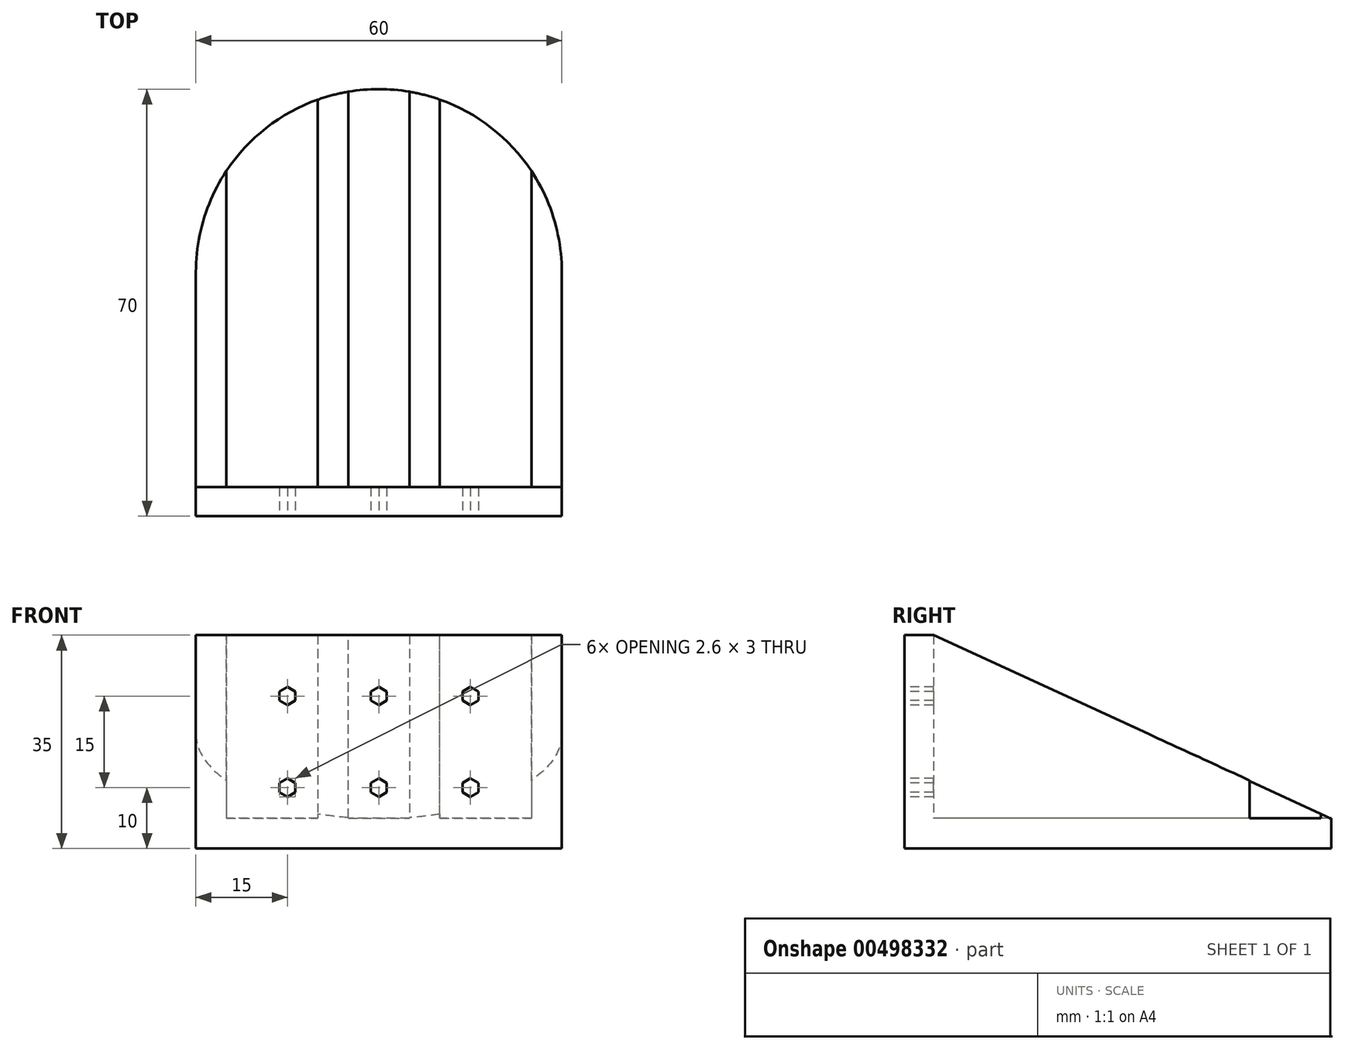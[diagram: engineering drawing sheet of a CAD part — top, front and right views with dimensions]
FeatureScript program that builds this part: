
annotation { "Feature Type Name" : "Feature", "Feature Type Description" : "" }
export const myFeature = defineFeature(function(context is Context, id is Id, definition is map)
    precondition{}
    {
        {
            var Q0;
            Q0=qCreatedBy(makeId("Top.planeOp"),FACE);
            var sketch = newSketch(context, id + "F0", { "sketchPlane" : qUnion([Q0])});
            skLineSegment(sketch, "E0.bottom", {"start": v(0, 0) * mm, "end": v(60, 0) * mm});
            skLineSegment(sketch, "E0.top", {"start": v(0, 70) * mm, "end": v(60, 70) * mm});
            skLineSegment(sketch, "E0.left", {"start": v(0, 0) * mm, "end": v(0, 70) * mm});
            skLineSegment(sketch, "E0.right", {"start": v(60, 0) * mm, "end": v(60, 70) * mm});
            skSolve(sketch);
        }
        {
            var Q0;
            Q0=makeQuery(id+"F0.imprint","IMPRINT",FACE,{"disambiguationData":[TD([[makeQuery(id+"F0.imprint","IMPRINT",EDGE,{"derivedFrom":sQuery(id+"F0.wireOp",EDGE,"E0.bottom")}),1.0]])]});
            extrude(context, id + "F1", {"entities" : qUnion([Q0]), "depth" : 5 * mm});
        }
        {
            var Q0;
            Q0=makeQuery(id+"F1.opExtrude","CAP_FACE",FACE,{"disambiguationData":[OSD([sQuery(id+"F0.wireOp",EDGE,"E0.bottom"),sQuery(id+"F0.wireOp",EDGE,"E0.top"),sQuery(id+"F0.wireOp",EDGE,"E0.left"),sQuery(id+"F0.wireOp",EDGE,"E0.right")])],"isStart":false});
            var sketch = newSketch(context, id + "F2", { "sketchPlane" : qUnion([Q0])});
            skLineSegment(sketch, "E1.bottom", {"start": v(0, 0) * mm, "end": v(60, 0) * mm});
            skLineSegment(sketch, "E1.top", {"start": v(0, 4.74) * mm, "end": v(60, 4.74) * mm});
            skLineSegment(sketch, "E1.left", {"start": v(0, 0) * mm, "end": v(0, 4.74) * mm});
            skLineSegment(sketch, "E1.right", {"start": v(60, 0) * mm, "end": v(60, 4.74) * mm});
            skSolve(sketch);
        }
        {
            var Q0;
            Q0 = qSketchRegion(id + "F2", true);
            extrude(context, id + "F3", {"entities" : qUnion([Q0]), "operationType" : NewBodyOperationType.ADD, "depth" : 30 * mm});
        }
        {
            var Q0;
            Q0=makeQuery(id+"F3.boolean.opBoolean","MERGE",FACE,{"derivedFrom":[makeQuery(id+"F1.opExtrude","SWEPT_FACE",FACE,{"disambiguationData":[OSD([sQuery(id+"F0.wireOp",EDGE,"E0.bottom")])]}),makeQuery(id+"F3.opExtrude","SWEPT_FACE",FACE,{"disambiguationData":[OSD([sQuery(id+"F2.wireOp",EDGE,"E1.bottom")])]})]});
            var sketch = newSketch(context, id + "F4", { "sketchPlane" : qUnion([Q0])});
            skLineSegment(sketch, "E2", {"start": v(0, 0) * mm, "end": v(30, 0) * mm});
            skLineSegment(sketch, "E3", {"start": v(30, 0) * mm, "end": v(30, 10) * mm});
            skLineSegment(sketch, "E4", {"start": v(30, 10) * mm, "end": v(45, 10) * mm});
            skLineSegment(sketch, "E5", {"start": v(45, 10) * mm, "end": v(30, 10) * mm});
            skLineSegment(sketch, "E6", {"start": v(30, 10) * mm, "end": v(15, 10) * mm});
            skLineSegment(sketch, "E7", {"start": v(15, 10) * mm, "end": v(15, 25) * mm});
            skLineSegment(sketch, "E8", {"start": v(15, 25) * mm, "end": v(30, 25) * mm});
            skLineSegment(sketch, "E9", {"start": v(30, 25) * mm, "end": v(45, 25) * mm});
            skLineSegment(sketch, "E10", {"start": v(15, 25) * mm, "end": v(15, 26.5) * mm});
            skCircle(sketch, "E11.cCircle", {"center": v(15, 25) * mm, "radius": 1.5 * mm, "construction": true});
            skLineSegment(sketch, "E11.0", {"start": v(15, 26.5) * mm, "end": v(16.3, 25.75) * mm});
            skLineSegment(sketch, "E11.1", {"start": v(16.3, 25.75) * mm, "end": v(16.3, 24.25) * mm});
            skLineSegment(sketch, "E11.2", {"start": v(16.3, 24.25) * mm, "end": v(15, 23.5) * mm});
            skLineSegment(sketch, "E11.3", {"start": v(15, 23.5) * mm, "end": v(13.7, 24.25) * mm});
            skLineSegment(sketch, "E11.4", {"start": v(13.7, 24.25) * mm, "end": v(13.7, 25.75) * mm});
            skLineSegment(sketch, "E11.5", {"start": v(13.7, 25.75) * mm, "end": v(15, 26.5) * mm});
            skLineSegment(sketch, "E12.0.1.0", {"start": v(16.3, 9.25) * mm, "end": v(15, 8.5) * mm});
            skLineSegment(sketch, "E12.0.1.1", {"start": v(16.3, 10.75) * mm, "end": v(16.3, 9.25) * mm});
            skLineSegment(sketch, "E12.0.1.2", {"start": v(15, 11.5) * mm, "end": v(16.3, 10.75) * mm});
            skCircle(sketch, "E12.0.1.3", {"center": v(15, 10) * mm, "radius": 1.5 * mm, "construction": true});
            skLineSegment(sketch, "E12.0.1.4", {"start": v(15, 8.5) * mm, "end": v(13.7, 9.25) * mm});
            skLineSegment(sketch, "E12.0.1.5", {"start": v(13.7, 9.25) * mm, "end": v(13.7, 10.75) * mm});
            skLineSegment(sketch, "E12.0.1.6", {"start": v(13.7, 10.75) * mm, "end": v(15, 11.5) * mm});
            skLineSegment(sketch, "E12.0.1.7", {"start": v(15, 10) * mm, "end": v(15, 11.5) * mm});
            skLineSegment(sketch, "E12.1.0.0", {"start": v(31.3, 24.25) * mm, "end": v(30, 23.5) * mm});
            skLineSegment(sketch, "E12.1.0.1", {"start": v(31.3, 25.75) * mm, "end": v(31.3, 24.25) * mm});
            skLineSegment(sketch, "E12.1.0.2", {"start": v(30, 26.5) * mm, "end": v(31.3, 25.75) * mm});
            skCircle(sketch, "E12.1.0.3", {"center": v(30, 25) * mm, "radius": 1.5 * mm, "construction": true});
            skLineSegment(sketch, "E12.1.0.4", {"start": v(30, 23.5) * mm, "end": v(28.7, 24.25) * mm});
            skLineSegment(sketch, "E12.1.0.5", {"start": v(28.7, 24.25) * mm, "end": v(28.7, 25.75) * mm});
            skLineSegment(sketch, "E12.1.0.6", {"start": v(28.7, 25.75) * mm, "end": v(30, 26.5) * mm});
            skLineSegment(sketch, "E12.1.0.7", {"start": v(30, 25) * mm, "end": v(30, 26.5) * mm});
            skLineSegment(sketch, "E12.1.1.0", {"start": v(31.3, 9.25) * mm, "end": v(30, 8.5) * mm});
            skLineSegment(sketch, "E12.1.1.1", {"start": v(31.3, 10.75) * mm, "end": v(31.3, 9.25) * mm});
            skLineSegment(sketch, "E12.1.1.2", {"start": v(30, 11.5) * mm, "end": v(31.3, 10.75) * mm});
            skCircle(sketch, "E12.1.1.3", {"center": v(30, 10) * mm, "radius": 1.5 * mm, "construction": true});
            skLineSegment(sketch, "E12.1.1.4", {"start": v(30, 8.5) * mm, "end": v(28.7, 9.25) * mm});
            skLineSegment(sketch, "E12.1.1.5", {"start": v(28.7, 9.25) * mm, "end": v(28.7, 10.75) * mm});
            skLineSegment(sketch, "E12.1.1.6", {"start": v(28.7, 10.75) * mm, "end": v(30, 11.5) * mm});
            skLineSegment(sketch, "E12.1.1.7", {"start": v(30, 10) * mm, "end": v(30, 11.5) * mm});
            skLineSegment(sketch, "E12.2.0.0", {"start": v(46.3, 24.25) * mm, "end": v(45, 23.5) * mm});
            skLineSegment(sketch, "E12.2.0.1", {"start": v(46.3, 25.75) * mm, "end": v(46.3, 24.25) * mm});
            skLineSegment(sketch, "E12.2.0.2", {"start": v(45, 26.5) * mm, "end": v(46.3, 25.75) * mm});
            skCircle(sketch, "E12.2.0.3", {"center": v(45, 25) * mm, "radius": 1.5 * mm, "construction": true});
            skLineSegment(sketch, "E12.2.0.4", {"start": v(45, 23.5) * mm, "end": v(43.7, 24.25) * mm});
            skLineSegment(sketch, "E12.2.0.5", {"start": v(43.7, 24.25) * mm, "end": v(43.7, 25.75) * mm});
            skLineSegment(sketch, "E12.2.0.6", {"start": v(43.7, 25.75) * mm, "end": v(45, 26.5) * mm});
            skLineSegment(sketch, "E12.2.0.7", {"start": v(45, 25) * mm, "end": v(45, 26.5) * mm});
            skLineSegment(sketch, "E12.2.1.0", {"start": v(46.3, 9.25) * mm, "end": v(45, 8.5) * mm});
            skLineSegment(sketch, "E12.2.1.1", {"start": v(46.3, 10.75) * mm, "end": v(46.3, 9.25) * mm});
            skLineSegment(sketch, "E12.2.1.2", {"start": v(45, 11.5) * mm, "end": v(46.3, 10.75) * mm});
            skCircle(sketch, "E12.2.1.3", {"center": v(45, 10) * mm, "radius": 1.5 * mm, "construction": true});
            skLineSegment(sketch, "E12.2.1.4", {"start": v(45, 8.5) * mm, "end": v(43.7, 9.25) * mm});
            skLineSegment(sketch, "E12.2.1.5", {"start": v(43.7, 9.25) * mm, "end": v(43.7, 10.75) * mm});
            skLineSegment(sketch, "E12.2.1.6", {"start": v(43.7, 10.75) * mm, "end": v(45, 11.5) * mm});
            skLineSegment(sketch, "E12.2.1.7", {"start": v(45, 10) * mm, "end": v(45, 11.5) * mm});
            skLineSegment(sketch, "E12.direction1", {"start": v(13.7, 24.25) * mm, "end": v(28.7, 24.25) * mm, "construction": true});
            skLineSegment(sketch, "E12.direction2", {"start": v(13.7, 24.25) * mm, "end": v(13.7, 9.25) * mm, "construction": true});
            skSolve(sketch);
        }
        {
            var Q0;
            {var subQ0=sQuery(id+"F4.wireOp",EDGE,"E10");Q0=makeQuery(id+"F4.imprint","IMPRINT",FACE,{"disambiguationData":[TD([[makeQuery(id+"F4.imprint","IMPRINT",EDGE,{"derivedFrom":subQ0}),1.0]])]});}
            var Q1;
            {var subQ3=sQuery(id+"F4.wireOp",EDGE,"E11.2");Q1=makeQuery(id+"F4.imprint","IMPRINT",FACE,{"disambiguationData":[TD([[makeQuery(id+"F4.imprint","IMPRINT",EDGE,{"derivedFrom":subQ3}),-1.0]])]});}
            var Q2;
            {var subQ0=sQuery(id+"F4.wireOp",EDGE,"E10");Q2=makeQuery(id+"F4.imprint","IMPRINT",FACE,{"disambiguationData":[TD([[makeQuery(id+"F4.imprint","IMPRINT",EDGE,{"derivedFrom":subQ0}),-1.0]])]});}
            var Q3;
            {var subQ0=sQuery(id+"F4.wireOp",EDGE,"E12.1.0.0");Q3=makeQuery(id+"F4.imprint","IMPRINT",FACE,{"disambiguationData":[TD([[makeQuery(id+"F4.imprint","IMPRINT",EDGE,{"derivedFrom":subQ0}),-1.0]])]});}
            var Q4;
            {var subQ4=sQuery(id+"F4.wireOp",EDGE,"E12.1.0.6");Q4=makeQuery(id+"F4.imprint","IMPRINT",FACE,{"disambiguationData":[TD([[makeQuery(id+"F4.imprint","IMPRINT",EDGE,{"derivedFrom":subQ4}),-1.0]])]});}
            var Q5;
            {var subQ4=sQuery(id+"F4.wireOp",EDGE,"E12.1.0.2");Q5=makeQuery(id+"F4.imprint","IMPRINT",FACE,{"disambiguationData":[TD([[makeQuery(id+"F4.imprint","IMPRINT",EDGE,{"derivedFrom":subQ4}),-1.0]])]});}
            var Q6;
            {var subQ4=sQuery(id+"F4.wireOp",EDGE,"E12.2.0.6");Q6=makeQuery(id+"F4.imprint","IMPRINT",FACE,{"disambiguationData":[TD([[makeQuery(id+"F4.imprint","IMPRINT",EDGE,{"derivedFrom":subQ4}),-1.0]])]});}
            var Q7;
            Q7=makeQuery(id+"F4.imprint","IMPRINT",FACE,{"disambiguationData":[TD([[makeQuery(id+"F4.imprint","IMPRINT",EDGE,{"derivedFrom":sQuery(id+"F4.wireOp",EDGE,"E12.2.0.0")}),-1.0]])]});
            var Q8;
            Q8=makeQuery(id+"F4.imprint","IMPRINT",FACE,{"disambiguationData":[TD([[makeQuery(id+"F4.imprint","IMPRINT",EDGE,{"derivedFrom":sQuery(id+"F4.wireOp",EDGE,"E12.2.1.0")}),-1.0]])]});
            var Q9;
            {var subQ4=sQuery(id+"F4.wireOp",EDGE,"E12.2.1.6");Q9=makeQuery(id+"F4.imprint","IMPRINT",FACE,{"disambiguationData":[TD([[makeQuery(id+"F4.imprint","IMPRINT",EDGE,{"derivedFrom":subQ4}),-1.0]])]});}
            var Q10;
            {var subQ3=sQuery(id+"F4.wireOp",EDGE,"E12.1.1.0");Q10=makeQuery(id+"F4.imprint","IMPRINT",FACE,{"disambiguationData":[TD([[makeQuery(id+"F4.imprint","IMPRINT",EDGE,{"derivedFrom":subQ3}),-1.0]])]});}
            var Q11;
            {var subQ3=sQuery(id+"F4.wireOp",EDGE,"E12.1.1.4");Q11=makeQuery(id+"F4.imprint","IMPRINT",FACE,{"disambiguationData":[TD([[makeQuery(id+"F4.imprint","IMPRINT",EDGE,{"derivedFrom":subQ3}),-1.0]])]});}
            var Q12;
            {var subQ4=sQuery(id+"F4.wireOp",EDGE,"E12.1.1.6");Q12=makeQuery(id+"F4.imprint","IMPRINT",FACE,{"disambiguationData":[TD([[makeQuery(id+"F4.imprint","IMPRINT",EDGE,{"derivedFrom":subQ4}),-1.0]])]});}
            var Q13;
            {var subQ4=sQuery(id+"F4.wireOp",EDGE,"E12.1.1.2");Q13=makeQuery(id+"F4.imprint","IMPRINT",FACE,{"disambiguationData":[TD([[makeQuery(id+"F4.imprint","IMPRINT",EDGE,{"derivedFrom":subQ4}),-1.0]])]});}
            var Q14;
            {var subQ1=sQuery(id+"F4.wireOp",EDGE,"E12.0.1.0");Q14=makeQuery(id+"F4.imprint","IMPRINT",FACE,{"disambiguationData":[TD([[makeQuery(id+"F4.imprint","IMPRINT",EDGE,{"derivedFrom":subQ1}),-1.0]])]});}
            var Q15;
            {var subQ4=sQuery(id+"F4.wireOp",EDGE,"E12.0.1.2");Q15=makeQuery(id+"F4.imprint","IMPRINT",FACE,{"disambiguationData":[TD([[makeQuery(id+"F4.imprint","IMPRINT",EDGE,{"derivedFrom":subQ4}),-1.0]])]});}
            extrude(context, id + "F5", {"entities" : qUnion([Q0, Q1, Q2, Q3, Q4, Q5, Q6, Q7, Q8, Q9, Q10, Q11, Q12, Q13, Q14, Q15]), "operationType" : NewBodyOperationType.REMOVE, "oppositeDirection" : true, "depth" : 25 * mm});
        }
        {
            var Q0;
            Q0=makeQuery(id+"F3.boolean.opBoolean","MERGE",FACE,{"derivedFrom":[makeQuery(id+"F1.opExtrude","SWEPT_FACE",FACE,{"disambiguationData":[OSD([sQuery(id+"F0.wireOp",EDGE,"E0.left")])]}),makeQuery(id+"F3.opExtrude","SWEPT_FACE",FACE,{"disambiguationData":[OSD([sQuery(id+"F2.wireOp",EDGE,"E1.left")])]})]});
            var sketch = newSketch(context, id + "F6", { "sketchPlane" : qUnion([Q0])});
            skLineSegment(sketch, "E13", {"start": v(-4.74, 35) * mm, "end": v(-4.74, 5) * mm});
            skLineSegment(sketch, "E14", {"start": v(-4.74, 5) * mm, "end": v(-70, 5) * mm});
            skLineSegment(sketch, "E15", {"start": v(-70, 5) * mm, "end": v(-4.74, 35) * mm});
            skSolve(sketch);
        }
        {
            var Q0;
            Q0 = qSketchRegion(id + "F6", true);
            extrude(context, id + "F7", {"entities" : qUnion([Q0]), "operationType" : NewBodyOperationType.ADD, "oppositeDirection" : true, "depth" : 5 * mm});
        }
        {
            var Q0;
            Q0=makeQuery(id+"F3.boolean.opBoolean","MERGE",FACE,{"derivedFrom":[makeQuery(id+"F1.opExtrude","SWEPT_FACE",FACE,{"disambiguationData":[OSD([sQuery(id+"F0.wireOp",EDGE,"E0.right")])]}),makeQuery(id+"F3.opExtrude","SWEPT_FACE",FACE,{"disambiguationData":[OSD([sQuery(id+"F2.wireOp",EDGE,"E1.right")])]})]});
            var sketch = newSketch(context, id + "F8", { "sketchPlane" : qUnion([Q0])});
            skLineSegment(sketch, "E16", {"start": v(4.74, 35) * mm, "end": v(4.74, 5) * mm});
            skLineSegment(sketch, "E17", {"start": v(4.74, 5) * mm, "end": v(70, 5) * mm});
            skLineSegment(sketch, "E18", {"start": v(70, 5) * mm, "end": v(4.74, 35) * mm});
            skSolve(sketch);
        }
        {
            var Q0;
            Q0 = qSketchRegion(id + "F8", true);
            extrude(context, id + "F9", {"entities" : qUnion([Q0]), "operationType" : NewBodyOperationType.ADD, "oppositeDirection" : true, "depth" : 5 * mm});
        }
        {
            var Q0;
            Q0=makeQuery(id+"F3.opExtrude","SWEPT_FACE",FACE,{"disambiguationData":[OSD([sQuery(id+"F2.wireOp",EDGE,"E1.top")])]});
            var sketch = newSketch(context, id + "F10", { "sketchPlane" : qUnion([Q0])});
            skLineSegment(sketch, "E19", {"start": v(-30, 35) * mm, "end": v(-30, 30) * mm});
            skLineSegment(sketch, "E20", {"start": v(-30, 30) * mm, "end": v(-25, 30) * mm});
            skLineSegment(sketch, "E21", {"start": v(-30, 30) * mm, "end": v(-35, 30) * mm});
            skLineSegment(sketch, "E22", {"start": v(-35, 30) * mm, "end": v(-35, 5) * mm});
            skLineSegment(sketch, "E23", {"start": v(-35, 30) * mm, "end": v(-35, 35) * mm});
            skLineSegment(sketch, "E24", {"start": v(-25, 30) * mm, "end": v(-25, 35) * mm});
            skLineSegment(sketch, "E25", {"start": v(-25, 30) * mm, "end": v(-25, 5) * mm});
            skLineSegment(sketch, "E26", {"start": v(-35, 5) * mm, "end": v(-40, 5) * mm});
            skLineSegment(sketch, "E27", {"start": v(-40, 5) * mm, "end": v(-40, 35) * mm});
            skLineSegment(sketch, "E28", {"start": v(-40, 35) * mm, "end": v(-35, 35) * mm});
            skLineSegment(sketch, "E29", {"start": v(-25, 35) * mm, "end": v(-20, 35) * mm});
            skLineSegment(sketch, "E30", {"start": v(-20, 35) * mm, "end": v(-20, 5) * mm});
            skLineSegment(sketch, "E31", {"start": v(-20, 5) * mm, "end": v(-25, 5) * mm});
            skSolve(sketch);
        }
        {
            var Q0;
            Q0=makeQuery(id+"F10.imprint","IMPRINT",FACE,{"disambiguationData":[TD([[makeQuery(id+"F10.imprint","IMPRINT",EDGE,{"derivedFrom":sQuery(id+"F10.wireOp",EDGE,"E22")}),-1.0]])]});
            var Q1;
            Q1=makeQuery(id+"F10.imprint","IMPRINT",FACE,{"disambiguationData":[TD([[makeQuery(id+"F10.imprint","IMPRINT",EDGE,{"derivedFrom":sQuery(id+"F10.wireOp",EDGE,"E24")}),-1.0]])]});
            extrude(context, id + "F11", {"entities" : qUnion([Q0, Q1]), "operationType" : NewBodyOperationType.ADD, "depth" : 65 * mm});
        }
        {
            var Q0;
            Q0=makeQuery(id+"F11.opExtrude","SWEPT_FACE",FACE,{"disambiguationData":[OSD([sQuery(id+"F10.wireOp",EDGE,"E30")])]});
            var sketch = newSketch(context, id + "F12", { "sketchPlane" : qUnion([Q0])});
            skLineSegment(sketch, "E32", {"start": v(-4.74, 35) * mm, "end": v(-69.74, 5) * mm});
            skLineSegment(sketch, "E33", {"start": v(-69.74, 5) * mm, "end": v(-69.74, 44.97) * mm});
            skLineSegment(sketch, "E34", {"start": v(-69.74, 44.97) * mm, "end": v(-4.74, 44.97) * mm});
            skLineSegment(sketch, "E35", {"start": v(-4.74, 44.97) * mm, "end": v(-4.74, 35) * mm});
            skSolve(sketch);
        }
        {
            var Q0;
            Q0 = qSketchRegion(id + "F12", true);
            extrude(context, id + "F13", {"entities" : qUnion([Q0]), "operationType" : NewBodyOperationType.REMOVE, "oppositeDirection" : true, "depth" : 25 * mm});
        }
        {
            var Q0;
            Q0=makeQuery(id+"F1.opExtrude","CAP_FACE",FACE,{"disambiguationData":[OSD([sQuery(id+"F0.wireOp",EDGE,"E0.bottom"),sQuery(id+"F0.wireOp",EDGE,"E0.top"),sQuery(id+"F0.wireOp",EDGE,"E0.left"),sQuery(id+"F0.wireOp",EDGE,"E0.right")])],"isStart":true});
            var sketch = newSketch(context, id + "F14", { "sketchPlane" : qUnion([Q0])});
            skLineSegment(sketch, "E36", {"start": v(30, -70) * mm, "end": v(30, -40) * mm});
            skLineSegment(sketch, "E37", {"start": v(30, -40) * mm, "end": v(0, -40) * mm});
            skLineSegment(sketch, "E38", {"start": v(30, -40) * mm, "end": v(60, -40) * mm});
            skArc(sketch, "E39", {"start": v(0, -40) * mm, "mid": v(30, -70) * mm, "end": v(60, -40) * mm});
            skLineSegment(sketch, "E40", {"start": v(0, -40) * mm, "end": v(-10, -40) * mm});
            skLineSegment(sketch, "E41", {"start": v(-10, -40) * mm, "end": v(-10, -80) * mm});
            skLineSegment(sketch, "E42", {"start": v(-10, -80) * mm, "end": v(70, -80) * mm});
            skLineSegment(sketch, "E43", {"start": v(70, -80) * mm, "end": v(70, -40) * mm});
            skLineSegment(sketch, "E44", {"start": v(70, -40) * mm, "end": v(60, -40) * mm});
            skSolve(sketch);
        }
        {
            var Q0;
            {var subQ0=sQuery(id+"F14.wireOp",EDGE,"E40");Q0=makeQuery(id+"F14.imprint","IMPRINT",FACE,{"disambiguationData":[TD([[makeQuery(id+"F14.imprint","IMPRINT",EDGE,{"derivedFrom":subQ0}),1.0]])]});}
            var Q1;
            {var subQ1=makeQuery(id+"F1.opExtrude","CAP_EDGE",EDGE,{"disambiguationData":[OSD([sQuery(id+"F0.wireOp",EDGE,"E0.top")])],"isStart":true});var subQ3=makeQuery(id+"F1.opExtrude","CAP_EDGE",EDGE,{"disambiguationData":[OSD([sQuery(id+"F0.wireOp",EDGE,"E0.left")])],"isStart":true});var subQ5=makeQuery(id+"F14.imprint","INTERSECT",VERTEX,{"derivedFrom":[subQ1,subQ3]});Q1=makeQuery(id+"F14.imprint","IMPRINT",FACE,{"disambiguationData":[TD([[makeQuery(id+"F14.imprint","IMPRINT",EDGE,{"disambiguationData":[TD([[subQ5,-1.0]])],"derivedFrom":subQ1}),1.0]])]});}
            var Q2;
            {var subQ1=makeQuery(id+"F1.opExtrude","CAP_EDGE",EDGE,{"disambiguationData":[OSD([sQuery(id+"F0.wireOp",EDGE,"E0.top")])],"isStart":true});var subQ3=makeQuery(id+"F1.opExtrude","CAP_EDGE",EDGE,{"disambiguationData":[OSD([sQuery(id+"F0.wireOp",EDGE,"E0.right")])],"isStart":true});var subQ5=makeQuery(id+"F14.imprint","INTERSECT",VERTEX,{"derivedFrom":[subQ1,subQ3]});Q2=makeQuery(id+"F14.imprint","IMPRINT",FACE,{"disambiguationData":[TD([[makeQuery(id+"F14.imprint","IMPRINT",EDGE,{"disambiguationData":[TD([[subQ5,1.0]])],"derivedFrom":subQ1}),1.0]])]});}
            extrude(context, id + "F15", {"entities" : qUnion([Q0, Q1, Q2]), "operationType" : NewBodyOperationType.REMOVE, "oppositeDirection" : true, "depth" : 25 * mm});
        }
    });
